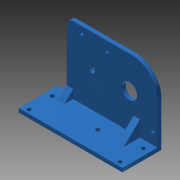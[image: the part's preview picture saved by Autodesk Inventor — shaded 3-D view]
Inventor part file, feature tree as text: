
AUTODESK INVENTOR PART (.ipt)
format: ipt  version: 2013 (Build 170138000, 138)  size: 171,008 bytes
history: native  units: mm
features: sketch x5, extrude x3, plane x2, fillet x2, rib x2, reference x1
ambient origin geometry x8: Origin, YZ Plane, XZ Plane, XY Plane, X Axis, Y Axis, Z Axis, Center Point
bodies: Solid1 (feature_tree)
feature tree (15):
  plane  "Work Plane1"
  extrude  "Extrusion2"  Depth=30.0mm
  sketch  "Sketch3"  dims[d4=5.0mm d5=29.0mm d8=30.0mm d10=4.0mm]
  extrude  "Extrusion3"  Depth=29.0mm
  fillet  "Fillet1"  Radius=30.0mm
  fillet  "Fillet2"  Radius=4.0mm
  extrude  "Extrusion4"  Depth=3.0mm TaperAngle=0.0deg
  plane  "Work Plane4"
  rib  "Rib1"
  rib  "Rib2"
  sketch  "Sketch1"  dims[d0=80.0mm d1=30.0mm]
  sketch  "Sketch4"  dims[d12=12.0mm d15=3.0mm d16=0.0mm]
  reference  "Reference1"
  sketch  "Sketch6"  dims[d17=50.0mm]
  sketch  "Sketch7"  dims[d19=3.0mm d20=3.0mm d21=3.0mm d22=3.0mm d25=5.0mm d26=3.0mm d27=100.0mm d28=10.0mm d29=20.0mm d30=38.0mm d31=18.0mm d32=30.0mm d33=49.0mm d34=20.0mm d35=-6.892mm d36=80.0mm d37=70.0mm d38=55.0mm d39=3.0mm d40=10.0mm d41=0.0mm d42=3.0mm d43=3.0mm d44=5.0mm d45=20.0mm d46=5.0mm d47=3.0mm d48=0.0mm d49=18.0mm d50=54.0mm d51=1.0mm d52=5.0mm d53=0.0mm d54=0.0mm d55=1.0mm d56=1.0mm d57=135.0deg d58=1.0mm d59=5.0mm d60=0.0mm d61=0.0mm d62=1.0mm d63=1.0mm]
